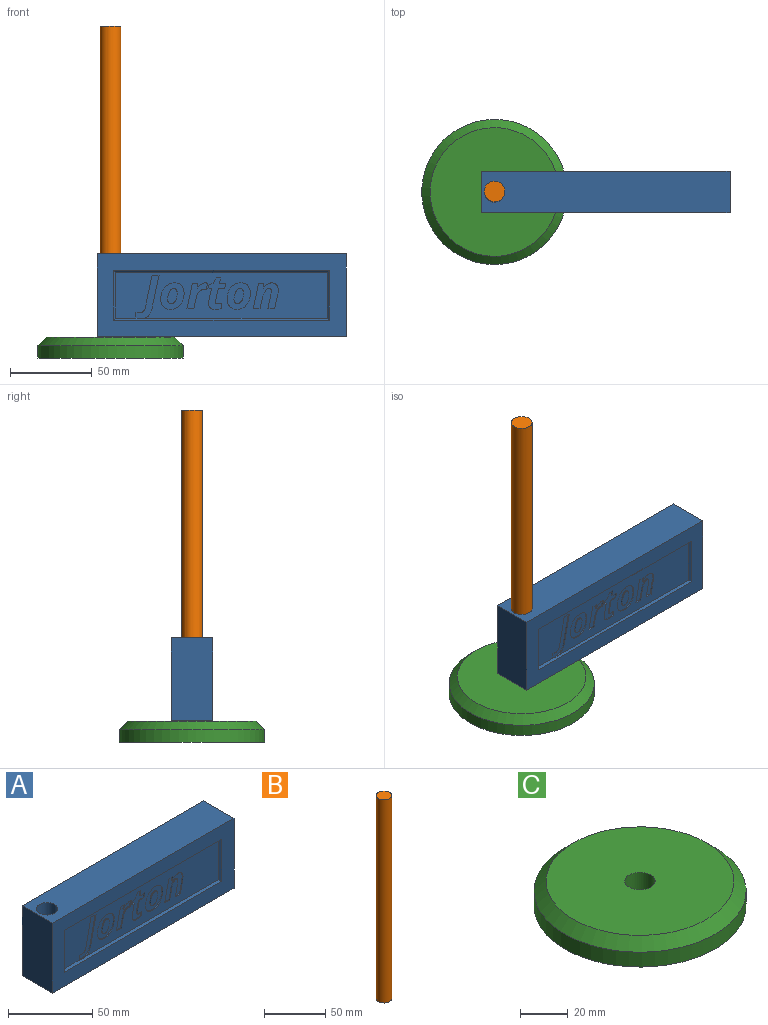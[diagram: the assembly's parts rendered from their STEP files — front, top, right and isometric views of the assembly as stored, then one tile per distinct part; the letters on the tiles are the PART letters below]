
ASSEMBLY  parts=3 mates=3
PART A: 115 faces, bbox 152.4x25.4x50.8 mm
  f0: plane 129.54x27.99mm, normal (0,-1,0), area 2792.4mm2, adj f8,f9,f10,f11,f12,f13,f14,f15
  f1: plane 152.4x50.8mm, normal (0,-1,0), area 3716.1mm2, adj f2,f3,f4,f5,f8,f9,f10,f11
  f2: plane 50.8x25.4mm, normal (1,0,0), area 1290.3mm2, adj f1,f3,f5,f6
  f3: plane 152.4x25.4mm, normal (0,0,1), area 3744.3mm2, adj f1,f2,f4,f6,f7
  f4: plane 50.8x25.4mm, normal (-1,0,0), area 1290.3mm2, adj f1,f3,f5,f6
  f5: plane 152.4x25.4mm, normal (0,0,-1), area 3744.3mm2, adj f1,f2,f4,f6,f7
  f6: plane 152.4x50.8mm, normal (0,1,0), area 7741.9mm2, adj f2,f3,f4,f5
  f7: cylinder r=6.35mm len=50.8mm, axis (0,0,1), area 2026.8mm2, adj f3,f5
  f8: plane 30.48x1.27mm, normal (0.71,-0.71,0), area 52.5mm2, adj f0,f1,f9,f10
  f9: plane 132.08x1.27mm, normal (0,-0.71,-0.71), area 234.9mm2, adj f0,f1,f8,f11
  f10: plane 132.08x1.27mm, normal (0,-0.71,0.71), area 234.9mm2, adj f0,f1,f8,f11,f23
  f11: plane 30.48x1.27mm, normal (-0.71,-0.71,0), area 52.5mm2, adj f0,f1,f9,f10
  f12: extruded ~2.61x0.76mm, area 2mm2, adj f0,f13,f21,f22,f23
  f13: extruded ~4.85x1.57mm, area 4mm2, adj f0,f12,f14,f22,f23
  f14: extruded ~4.99x2.45mm, area 4.3mm2, adj f0,f13,f15,f22
  f15: plane 19.9x4.24mm, normal (-0.98,0,0.21), area 15.5mm2, adj f0,f14,f16,f22
  f16: plane 4.26x0.76mm, normal (0,0,-1), area 3.2mm2, adj f0,f15,f17,f22
  f17: plane 19.3x4.09mm, normal (0.98,0,-0.21), area 15mm2, adj f0,f16,f18,f22
  f18: extruded ~2.68x1.25mm, area 2.3mm2, adj f0,f17,f19,f22
  f19: extruded ~2.25x0.85mm, area 1.9mm2, adj f0,f18,f20,f22
  f20: extruded ~2.29x0.76mm, area 1.8mm2, adj f0,f19,f21,f22
  f21: plane 3.54x0.76mm, normal (1,0,0), area 2.7mm2, adj f0,f12,f20,f22
  f22: plane 26.46x14.15mm, normal (0,-1,0), area 125mm2, adj f12,f13,f14,f15,f16,f17,f18,f19
  f23: plane 5.37x0.42mm, normal (0,1,0), area 1.3mm2, adj f10,f12,f13
  f24: extruded ~1.34x0.76mm, area 1mm2, adj f0,f25,f35,f36
  f25: extruded ~4.94x3.19mm, area 4.7mm2, adj f0,f24,f26,f36
  f26: plane 0.76x0.09mm, normal (0,0,-1), area 0.1mm2, adj f0,f25,f27,f36
  f27: plane 2.9x0.76mm, normal (-0.99,0,0.1), area 2.2mm2, adj f0,f26,f28,f36
  f28: plane 3.22x0.76mm, normal (0,0,-1), area 2.5mm2, adj f0,f27,f29,f36
  f29: plane 15.63x3.31mm, normal (0.98,0,-0.21), area 12.2mm2, adj f0,f28,f30,f36
  f30: plane 4.21x0.76mm, normal (0,0,1), area 3.2mm2, adj f0,f29,f31,f36
  f31: plane 6.99x1.49mm, normal (-0.98,0,0.21), area 5.4mm2, adj f0,f30,f32,f36
  f32: extruded ~3.67x1.74mm, area 3.1mm2, adj f0,f31,f33,f36
  f33: extruded ~2.85x1.28mm, area 2.4mm2, adj f0,f32,f34,f36
  f34: extruded ~1.4x0.76mm, area 1.1mm2, adj f0,f33,f35,f36
  f35: plane 4.05x0.92mm, normal (-0.98,0,0.22), area 3.2mm2, adj f0,f24,f34,f36
  f36: plane 15.93x12.6mm, normal (0,-1,0), area 84.8mm2, adj f24,f25,f26,f27,f28,f29,f30,f31
  f37: extruded ~5.23x0.99mm, area 4.1mm2, adj f0,f38,f54,f55
  f38: extruded ~4.54x1.6mm, area 3.8mm2, adj f0,f37,f39,f55
  f39: extruded ~4.33x1.65mm, area 3.6mm2, adj f0,f38,f40,f55
  f40: extruded ~4.42x1.28mm, area 3.6mm2, adj f0,f39,f41,f55
  f41: extruded ~3.61x2.89mm, area 3.6mm2, adj f0,f40,f42,f55
  f42: extruded ~5.31x1mm, area 4.1mm2, adj f0,f41,f43,f55
  f43: extruded ~4.37x1.63mm, area 3.7mm2, adj f0,f42,f44,f55
  f44: extruded ~4.36x1.64mm, area 3.6mm2, adj f0,f43,f45,f55
  f45: extruded ~4.42x1.25mm, area 3.6mm2, adj f0,f44,f54,f55
  f46: extruded ~2.76x2mm, area 3mm2, adj f47,f53,f55,f56
  f47: extruded ~3.33x0.76mm, area 2.6mm2, adj f46,f48,f55,f56
  f48: extruded ~2.39x1.31mm, area 2.1mm2, adj f47,f49,f55,f56
  f49: extruded ~1.89x0.86mm, area 1.6mm2, adj f48,f50,f55,f56
  f50: extruded ~2.59x2.1mm, area 2.9mm2, adj f49,f51,f55,f56
  f51: extruded ~3.4x0.76mm, area 2.6mm2, adj f50,f52,f55,f56
  f52: extruded ~2.5x1.36mm, area 2.2mm2, adj f51,f53,f55,f56
  f53: extruded ~1.88x0.85mm, area 1.6mm2, adj f46,f52,f55,f56
  f54: extruded ~3.53x2.85mm, area 3.5mm2, adj f0,f37,f45,f55
  f55: plane 16.21x14.24mm, normal (0,-1,0), area 143.7mm2, adj f37,f38,f39,f40,f41,f42,f43,f44
  f56: plane 9.34x5.76mm, normal (0,-1,0), area 41.7mm2, adj f46,f47,f48,f49,f50,f51,f52,f53
  f57: extruded ~5.23x0.99mm, area 4.1mm2, adj f0,f58,f74,f75
  f58: extruded ~4.54x1.6mm, area 3.8mm2, adj f0,f57,f59,f75
  f59: extruded ~4.33x1.65mm, area 3.6mm2, adj f0,f58,f60,f75
  f60: extruded ~4.42x1.28mm, area 3.6mm2, adj f0,f59,f61,f75
  f61: extruded ~3.61x2.89mm, area 3.6mm2, adj f0,f60,f62,f75
  f62: extruded ~5.31x1mm, area 4.1mm2, adj f0,f61,f63,f75
  f63: extruded ~4.37x1.63mm, area 3.7mm2, adj f0,f62,f64,f75
  f64: extruded ~4.36x1.64mm, area 3.6mm2, adj f0,f63,f65,f75
  f65: extruded ~4.42x1.25mm, area 3.6mm2, adj f0,f64,f74,f75
  f66: extruded ~2.76x2mm, area 3mm2, adj f67,f73,f75,f76
  f67: extruded ~3.33x0.76mm, area 2.6mm2, adj f66,f68,f75,f76
  f68: extruded ~2.39x1.31mm, area 2.1mm2, adj f67,f69,f75,f76
  f69: extruded ~1.89x0.86mm, area 1.6mm2, adj f68,f70,f75,f76
  f70: extruded ~2.59x2.1mm, area 2.9mm2, adj f69,f71,f75,f76
  f71: extruded ~3.4x0.76mm, area 2.6mm2, adj f70,f72,f75,f76
  f72: extruded ~2.5x1.36mm, area 2.2mm2, adj f71,f73,f75,f76
  f73: extruded ~1.88x0.85mm, area 1.6mm2, adj f66,f72,f75,f76
  f74: extruded ~3.53x2.85mm, area 3.5mm2, adj f0,f57,f65,f75
  f75: plane 16.21x14.24mm, normal (0,-1,0), area 143.7mm2, adj f57,f58,f59,f60,f61,f62,f63,f64
  f76: plane 9.34x5.76mm, normal (0,-1,0), area 41.7mm2, adj f66,f67,f68,f69,f70,f71,f72,f73
  f77: plane 4.21x0.76mm, normal (0,0,1), area 3.2mm2, adj f0,f78,f93,f94
  f78: plane 8.91x1.86mm, normal (-0.98,0,0.2), area 6.9mm2, adj f0,f77,f79,f94
  f79: extruded ~2.51x0.76mm, area 1.9mm2, adj f0,f78,f80,f94
  f80: extruded ~3.34x1.06mm, area 2.7mm2, adj f0,f79,f81,f94
  f81: extruded ~2.98x1.17mm, area 2.5mm2, adj f0,f80,f82,f94
  f82: extruded ~4.97x3.19mm, area 4.7mm2, adj f0,f81,f83,f94
  f83: plane 0.76x0.09mm, normal (0,0,-1), area 0.1mm2, adj f0,f82,f84,f94
  f84: plane 2.9x0.76mm, normal (-0.99,0,0.1), area 2.2mm2, adj f0,f83,f85,f94
  f85: plane 3.22x0.76mm, normal (0,0,-1), area 2.5mm2, adj f0,f84,f86,f94
  f86: plane 15.63x3.31mm, normal (0.98,0,-0.21), area 12.2mm2, adj f0,f85,f87,f94
  f87: plane 4.21x0.76mm, normal (0,0,1), area 3.2mm2, adj f0,f86,f88,f94
  f88: plane 6.48x1.37mm, normal (-0.98,0,0.21), area 5mm2, adj f0,f87,f89,f94
  f89: extruded ~4.45x1.65mm, area 3.6mm2, adj f0,f88,f90,f94
  f90: extruded ~2.33x1.6mm, area 2.2mm2, adj f0,f89,f91,f94
  f91: extruded ~1.72x1.51mm, area 2mm2, adj f0,f90,f92,f94
  f92: extruded ~1.66x0.76mm, area 1.3mm2, adj f0,f91,f93,f94
  f93: plane 9.13x1.92mm, normal (0.98,0,-0.21), area 7.1mm2, adj f0,f77,f92,f94
  f94: plane 15.93x15.33mm, normal (0,-1,0), area 142mm2, adj f77,f78,f79,f80,f81,f82,f83,f84
  f95: extruded ~2.27x0.76mm, area 1.8mm2, adj f0,f96,f113,f114
  f96: extruded ~1.23x1.03mm, area 1.4mm2, adj f0,f95,f97,f114
  f97: extruded ~0.76x0.74mm, area 0.6mm2, adj f0,f96,f98,f114
  f98: plane 7.54x1.61mm, normal (-0.98,0,0.21), area 5.9mm2, adj f0,f97,f99,f114
  f99: plane 3.95x0.76mm, normal (0,0,1), area 3mm2, adj f0,f98,f100,f114
  f100: plane 3.2x0.76mm, normal (-0.98,0,0.21), area 2.5mm2, adj f0,f99,f101,f114
  f101: plane 3.96x0.76mm, normal (0,0,-1), area 3mm2, adj f0,f100,f102,f114
  f102: plane 3.33x0.76mm, normal (-0.98,0,0.2), area 2.6mm2, adj f0,f101,f103,f114
  f103: plane 2.72x0.76mm, normal (0,0,-1), area 2.1mm2, adj f0,f102,f104,f114
  f104: plane 3.3x1.84mm, normal (0.87,0,-0.49), area 2.9mm2, adj f0,f103,f105,f114
  f105: plane 2.74x1.17mm, normal (0.39,0,-0.92), area 2.3mm2, adj f0,f104,f106,f114
  f106: plane 2.06x0.76mm, normal (0.98,0,-0.19), area 1.6mm2, adj f0,f105,f107,f114
  f107: plane 2.13x0.76mm, normal (0,0,1), area 1.6mm2, adj f0,f106,f108,f114
  f108: plane 7.54x1.61mm, normal (0.98,0,-0.21), area 5.9mm2, adj f0,f107,f109,f114
  f109: extruded ~1.57x0.76mm, area 1.2mm2, adj f0,f108,f110,f114
  f110: extruded ~2.73x0.99mm, area 2.3mm2, adj f0,f109,f111,f114
  f111: extruded ~3.08x0.88mm, area 2.5mm2, adj f0,f110,f112,f114
  f112: extruded ~3.72x0.76mm, area 2.9mm2, adj f0,f111,f113,f114
  f113: plane 3.15x0.76mm, normal (-1,0,0), area 2.4mm2, adj f0,f95,f112,f114
  f114: plane 19.25x10.98mm, normal (0,-1,0), area 105.8mm2, adj f95,f96,f97,f98,f99,f100,f101,f102
PART B: 3 faces, bbox 12.7x12.7x203.2 mm
  f0: cylinder r=6.35mm len=203.2mm, axis (0,0,-1), area 8107.3mm2, adj f1,f2
  f1: plane 12.7x12.7mm, normal (0,0,1), area 126.7mm2, adj f0
  f2: plane 12.7x12.7mm, normal (0,0,-1), area 126.7mm2, adj f0
PART C: 6 faces, bbox 88.9x88.9x12.7 mm
  f0: cylinder r=44.45mm len=88.9mm, axis (0,0,-1), area 2128.2mm2, adj f2,f3
  f1: plane 78.74x78.74mm, normal (0,0,1), area 4742.8mm2, adj f3,f4
  f2: plane 88.9x88.9mm, normal (0,0,-1), area 6207.2mm2, adj f0
  f3: cone r=39.37mm half-angle=45deg, axis (0,0,-1), area 1891.8mm2, adj f0,f1
  f4: cylinder r=6.35mm len=12.7mm, axis (0,0,1), area 505.7mm2, adj f1,f5
  f5: plane 12.7x12.7mm, normal (0,0,1), area 126.7mm2, adj f4
PLACE A rot(axis=(1,0,0),0deg) t=(67.98,0,25.66)mm
PLACE B rot(axis=(1,0,0),180deg) t=(0,0,88.93)mm
PLACE C rot(axis=(1,0,0),0deg) t=(0,0,-12.7)mm
MATE slider B.f0 <-> A.f7  axis (0,0,1) through (0,0,88.93)mm
MATE fastened B.f0 <-> C.f4  axis (0,0,-1) through (0,0,-12.67)mm
MATE cylindrical A.f7 <-> B.f0  axis (0,0,1) through (0,0,51.06)mm
